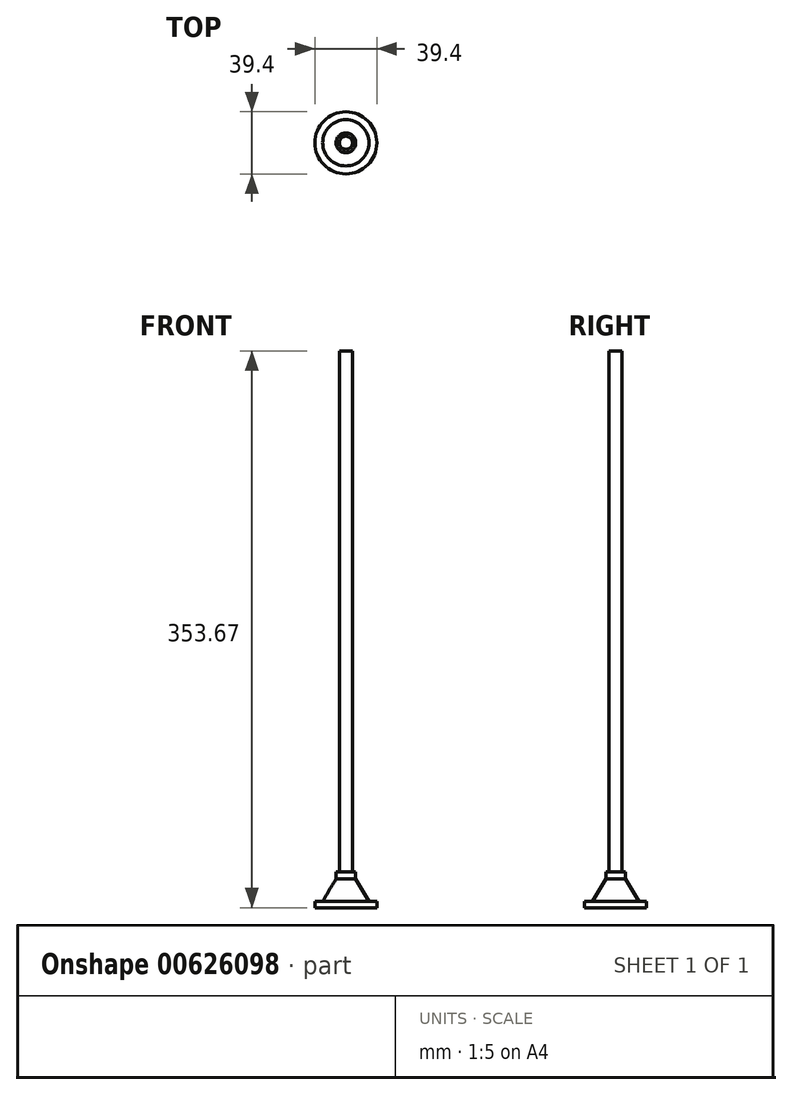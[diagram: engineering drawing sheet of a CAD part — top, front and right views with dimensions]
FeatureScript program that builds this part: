
annotation { "Feature Type Name" : "Feature", "Feature Type Description" : "" }
export const myFeature = defineFeature(function(context is Context, id is Id, definition is map)
    precondition{}
    {
        {
            var Q0;
            Q0=qCreatedBy(makeId("Front.planeOp"),FACE);
            var sketch = newSketch(context, id + "F0", { "sketchPlane" : qUnion([Q0])});
            skLineSegment(sketch, "E0.top", {"start": v(0, 331) * mm, "end": v(-4.15, 331) * mm});
            skLineSegment(sketch, "E0.left", {"start": v(0, 0) * mm, "end": v(0, 331) * mm});
            skLineSegment(sketch, "E0.right", {"start": v(-4.15, 0) * mm, "end": v(-4.15, 331) * mm});
            skLineSegment(sketch, "E1.bottom", {"start": v(0, 0) * mm, "end": v(2.1, 0) * mm});
            skLineSegment(sketch, "E1.left", {"start": v(-4.15, 0) * mm, "end": v(-4.15, -4.38) * mm});
            skLineSegment(sketch, "E1.right", {"start": v(2.1, 0) * mm, "end": v(2.1, -4.3) * mm});
            skLineSegment(sketch, "E2", {"start": v(2.1, -4.3) * mm, "end": v(10.55, -18.47) * mm});
            skLineSegment(sketch, "E3", {"start": v(-4.15, -4.38) * mm, "end": v(-4.15, -18.47) * mm});
            skLineSegment(sketch, "E4.bottom", {"start": v(10.55, -18.47) * mm, "end": v(15.55, -18.47) * mm});
            skLineSegment(sketch, "E4.top", {"start": v(-4.15, -22.67) * mm, "end": v(15.55, -22.67) * mm});
            skLineSegment(sketch, "E4.left", {"start": v(-4.15, -18.47) * mm, "end": v(-4.15, -22.67) * mm});
            skLineSegment(sketch, "E4.right", {"start": v(15.55, -18.47) * mm, "end": v(15.55, -22.67) * mm});
            skSolve(sketch);
        }
        {
            var Q0;
            Q0=makeQuery(id+"F0.imprint","IMPRINT",FACE,{"disambiguationData":[TD([[makeQuery(id+"F0.imprint","IMPRINT",EDGE,{"derivedFrom":sQuery(id+"F0.wireOp",EDGE,"E0.top")}),1.0]])]});
            var Q1;
            Q1=sQuery(id+"F0.wireOp",EDGE,"E0.right");
            revolve(context, id + "F1", {"entities" : qUnion([Q0]), "axis" : qUnion([Q1]), "revolveType" : RevolveType.FULL});
        }
    });
